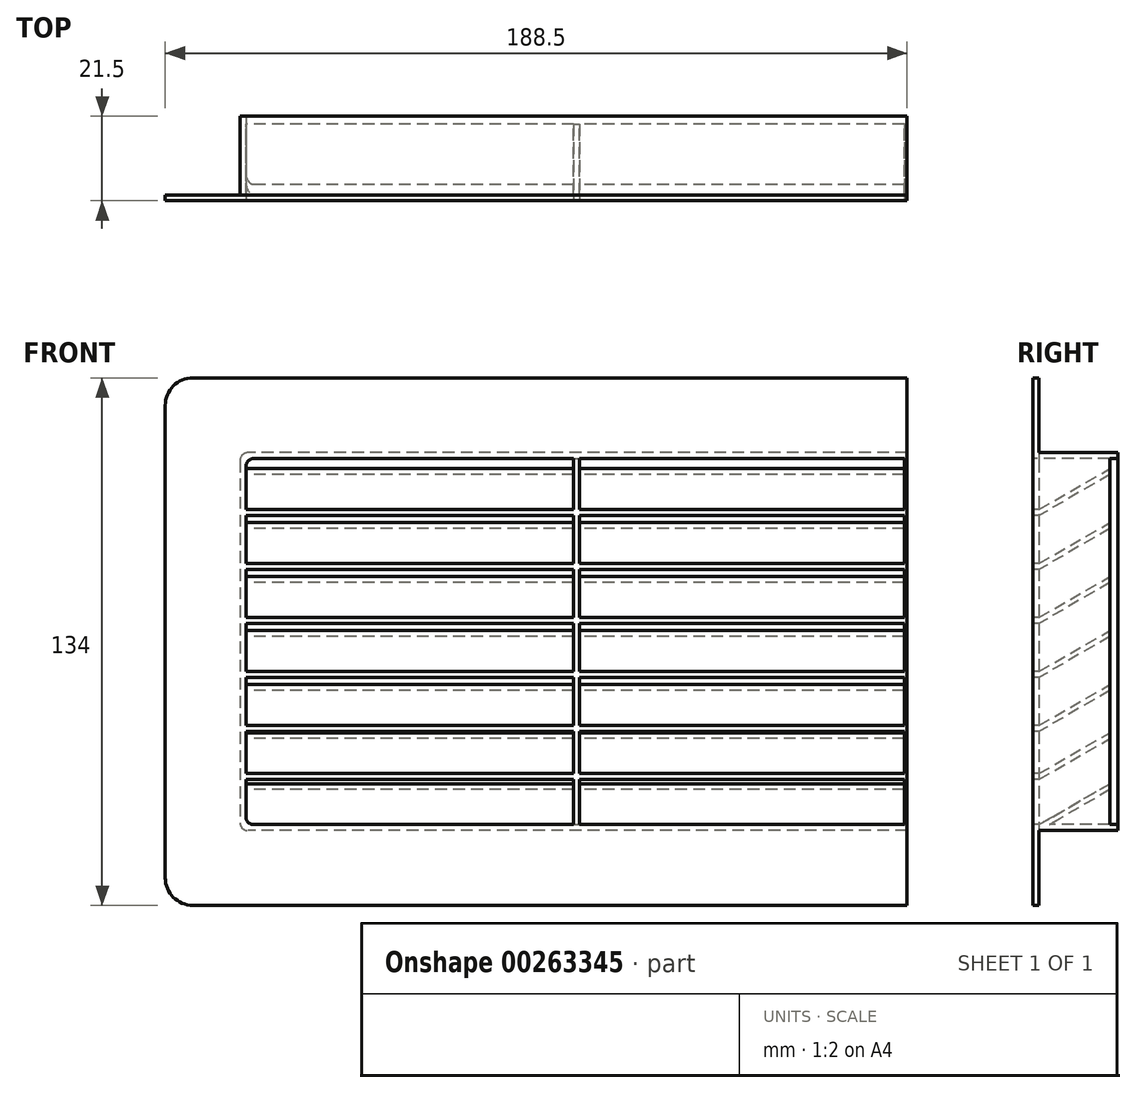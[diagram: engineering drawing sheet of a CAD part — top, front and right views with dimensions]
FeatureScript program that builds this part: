
annotation { "Feature Type Name" : "Feature", "Feature Type Description" : "" }
export const myFeature = defineFeature(function(context is Context, id is Id, definition is map)
    precondition{}
    {
        {
            var Q0;
            Q0=qCreatedBy(makeId("Front.planeOp"),FACE);
            var sketch = newSketch(context, id + "F0", { "sketchPlane" : qUnion([Q0])});
            skLineSegment(sketch, "E0.bottom", {"start": v(-180, 65) * mm, "end": v(180, 65) * mm});
            skLineSegment(sketch, "E0.top", {"start": v(-180, -65) * mm, "end": v(180, -65) * mm});
            skLineSegment(sketch, "E0.left", {"start": v(-185, 60) * mm, "end": v(-185, -60) * mm});
            skLineSegment(sketch, "E0.right", {"start": v(185, 60) * mm, "end": v(185, -60) * mm});
            skPoint(sketch, "E0.middle", {"position": v(0, 0) * mm});
            skPoint(sketch, "E1.visualSharp", {"position": v(-185, 65) * mm});
            skArc(sketch, "E1.filletArc", {"start": v(-180, 65) * mm, "mid": v(-183.54, 63.54) * mm, "end": v(-185, 60) * mm});
            skPoint(sketch, "E2.visualSharp", {"position": v(185, 65) * mm});
            skArc(sketch, "E2.filletArc", {"start": v(185, 60) * mm, "mid": v(183.54, 63.54) * mm, "end": v(180, 65) * mm});
            skPoint(sketch, "E3.visualSharp", {"position": v(185, -65) * mm});
            skArc(sketch, "E3.filletArc", {"start": v(180, -65) * mm, "mid": v(183.54, -63.54) * mm, "end": v(185, -60) * mm});
            skPoint(sketch, "E4.visualSharp", {"position": v(-185, -65) * mm});
            skArc(sketch, "E4.filletArc", {"start": v(-185, -60) * mm, "mid": v(-183.54, -63.54) * mm, "end": v(-180, -65) * mm});
            skSolve(sketch);
        }
        {
            var Q0;
            Q0=qSketchRegion(id+"F0",true);
            extrude(context, id + "F1", {"entities" : qUnion([Q0]), "depth" : 1.5 * mm});
        }
        {
            var Q0;
            Q0=makeQuery(id+"F1.opExtrude","CAP_FACE",FACE,{"disambiguationData":[OSD([sQuery(id+"F0.wireOp",EDGE,"E0.bottom"),sQuery(id+"F0.wireOp",EDGE,"E0.top"),sQuery(id+"F0.wireOp",EDGE,"E0.left"),sQuery(id+"F0.wireOp",EDGE,"E0.right")])],"isStart":false});
            var sketch = newSketch(context, id + "F2", { "sketchPlane" : qUnion([Q0])});
            skLineSegment(sketch, "E5.bottom", {"start": v(-166.5, 46.5) * mm, "end": v(-83.25, 46.5) * mm});
            skLineSegment(sketch, "E5.top", {"start": v(-166.5, -46.5) * mm, "end": v(-83.25, -46.5) * mm});
            skLineSegment(sketch, "E5.left", {"start": v(-166.5, 46.5) * mm, "end": v(-166.5, 33.54) * mm});
            skLineSegment(sketch, "E5.right", {"start": v(166.5, 46.5) * mm, "end": v(166.5, 33.54) * mm});
            skPoint(sketch, "E5.middle", {"position": v(0, 0) * mm});
            skLineSegment(sketch, "E6.0", {"start": v(-166.5, 32.04) * mm, "end": v(-83.25, 32.04) * mm});
            skLineSegment(sketch, "E7.0", {"start": v(-166.5, 18.32) * mm, "end": v(-83.25, 18.32) * mm});
            skLineSegment(sketch, "E8.0", {"start": v(-166.5, 4.6) * mm, "end": v(-83.25, 4.6) * mm});
            skLineSegment(sketch, "E9.0", {"start": v(-166.5, -9.1) * mm, "end": v(-83.25, -9.1) * mm});
            skLineSegment(sketch, "E10.0", {"start": v(-166.5, -22.82) * mm, "end": v(-83.25, -22.82) * mm});
            skLineSegment(sketch, "E11.0", {"start": v(-166.5, -33.54) * mm, "end": v(-83.25, -33.54) * mm});
            skLineSegment(sketch, "E12.0", {"start": v(-166.5, 33.54) * mm, "end": v(-83.25, 33.54) * mm});
            skLineSegment(sketch, "E13.0", {"start": v(-166.5, 19.82) * mm, "end": v(-83.25, 19.82) * mm});
            skLineSegment(sketch, "E14.0", {"start": v(-166.5, 6.1) * mm, "end": v(-83.25, 6.1) * mm});
            skLineSegment(sketch, "E15.0", {"start": v(-166.5, -7.6) * mm, "end": v(-83.25, -7.6) * mm});
            skLineSegment(sketch, "E16.0", {"start": v(-166.5, -21.32) * mm, "end": v(-83.25, -21.32) * mm});
            skLineSegment(sketch, "E17.0", {"start": v(-166.5, -35.04) * mm, "end": v(-83.25, -35.04) * mm});
            skLineSegment(sketch, "E18.0", {"start": v(-83.25, 46.5) * mm, "end": v(-83.25, 33.54) * mm});
            skLineSegment(sketch, "E19.0", {"start": v(-81.75, 46.5) * mm, "end": v(-81.75, 33.54) * mm});
            skLineSegment(sketch, "E20.0", {"start": v(0.75, 46.5) * mm, "end": v(0.75, 33.54) * mm});
            skLineSegment(sketch, "E21.0", {"start": v(2.25, 46.5) * mm, "end": v(2.25, 33.54) * mm});
            skLineSegment(sketch, "E22.0", {"start": v(84.75, 46.5) * mm, "end": v(84.75, 33.54) * mm});
            skLineSegment(sketch, "E23.0", {"start": v(86.25, 46.5) * mm, "end": v(86.25, 33.54) * mm});
            skLineSegment(sketch, "E24.trimOffspring", {"start": v(-81.75, 19.82) * mm, "end": v(0.75, 19.82) * mm});
            skLineSegment(sketch, "E25.trimOffspring", {"start": v(-81.75, 18.32) * mm, "end": v(0.75, 18.32) * mm});
            skLineSegment(sketch, "E26.trimOffspring", {"start": v(-81.75, 33.54) * mm, "end": v(0.75, 33.54) * mm});
            skLineSegment(sketch, "E27.trimOffspring", {"start": v(-81.75, 32.04) * mm, "end": v(0.75, 32.04) * mm});
            skLineSegment(sketch, "E28.trimOffspring", {"start": v(-83.25, 32.04) * mm, "end": v(-83.25, 19.82) * mm});
            skLineSegment(sketch, "E29.trimOffspring", {"start": v(-81.75, 32.04) * mm, "end": v(-81.75, 19.82) * mm});
            skLineSegment(sketch, "E30.trimOffspring", {"start": v(-166.5, 32.04) * mm, "end": v(-166.5, 19.82) * mm});
            skLineSegment(sketch, "E31.trimOffspring", {"start": v(-166.5, 18.32) * mm, "end": v(-166.5, 6.1) * mm});
            skLineSegment(sketch, "E32.trimOffspring", {"start": v(-81.75, 18.32) * mm, "end": v(-81.75, 6.1) * mm});
            skLineSegment(sketch, "E33.trimOffspring", {"start": v(-83.25, 18.32) * mm, "end": v(-83.25, 6.1) * mm});
            skLineSegment(sketch, "E34.trimOffspring", {"start": v(-83.25, 4.6) * mm, "end": v(-83.25, -7.6) * mm});
            skLineSegment(sketch, "E35.trimOffspring", {"start": v(-81.75, 4.6) * mm, "end": v(-81.75, -7.6) * mm});
            skLineSegment(sketch, "E36.trimOffspring", {"start": v(-81.75, 4.6) * mm, "end": v(0.75, 4.6) * mm});
            skLineSegment(sketch, "E37.trimOffspring", {"start": v(-81.75, 6.1) * mm, "end": v(0.75, 6.1) * mm});
            skLineSegment(sketch, "E38.trimOffspring", {"start": v(-166.5, 4.6) * mm, "end": v(-166.5, -7.6) * mm});
            skLineSegment(sketch, "E39.trimOffspring", {"start": v(-166.5, -9.1) * mm, "end": v(-166.5, -21.32) * mm});
            skLineSegment(sketch, "E40.trimOffspring", {"start": v(-83.25, -9.1) * mm, "end": v(-83.25, -21.32) * mm});
            skLineSegment(sketch, "E41.trimOffspring", {"start": v(-81.75, -9.1) * mm, "end": v(-81.75, -21.32) * mm});
            skLineSegment(sketch, "E42.trimOffspring", {"start": v(-81.75, -7.6) * mm, "end": v(0.75, -7.6) * mm});
            skLineSegment(sketch, "E43.trimOffspring", {"start": v(-81.75, -9.1) * mm, "end": v(0.75, -9.1) * mm});
            skLineSegment(sketch, "E44.trimOffspring", {"start": v(-166.5, -22.82) * mm, "end": v(-166.5, -33.54) * mm});
            skLineSegment(sketch, "E45.trimOffspring", {"start": v(-166.5, -35.04) * mm, "end": v(-166.5, -46.5) * mm});
            skLineSegment(sketch, "E46.trimOffspring", {"start": v(-83.25, -22.82) * mm, "end": v(-83.25, -33.54) * mm});
            skLineSegment(sketch, "E47.trimOffspring", {"start": v(-81.75, -22.82) * mm, "end": v(0.75, -22.82) * mm});
            skLineSegment(sketch, "E48.trimOffspring", {"start": v(-81.75, -21.32) * mm, "end": v(0.75, -21.32) * mm});
            skLineSegment(sketch, "E49.trimOffspring", {"start": v(-81.75, -22.82) * mm, "end": v(-81.75, -33.54) * mm});
            skLineSegment(sketch, "E50.trimOffspring", {"start": v(-83.25, -35.04) * mm, "end": v(-83.25, -46.5) * mm});
            skLineSegment(sketch, "E51.trimOffspring", {"start": v(-81.75, -35.04) * mm, "end": v(0.75, -35.04) * mm});
            skLineSegment(sketch, "E52.trimOffspring", {"start": v(-81.75, -33.54) * mm, "end": v(0.75, -33.54) * mm});
            skLineSegment(sketch, "E53.trimOffspring", {"start": v(-81.75, -35.04) * mm, "end": v(-81.75, -46.5) * mm});
            skLineSegment(sketch, "E54.trimOffspring", {"start": v(-81.75, -46.5) * mm, "end": v(0.75, -46.5) * mm});
            skLineSegment(sketch, "E55.trimOffspring", {"start": v(-81.75, 46.5) * mm, "end": v(0.75, 46.5) * mm});
            skLineSegment(sketch, "E56.trimOffspring", {"start": v(2.25, 46.5) * mm, "end": v(84.75, 46.5) * mm});
            skLineSegment(sketch, "E57.trimOffspring", {"start": v(2.25, 32.04) * mm, "end": v(84.75, 32.04) * mm});
            skLineSegment(sketch, "E58.trimOffspring", {"start": v(2.25, 33.54) * mm, "end": v(84.75, 33.54) * mm});
            skLineSegment(sketch, "E59.trimOffspring", {"start": v(2.25, 32.04) * mm, "end": v(2.25, 19.82) * mm});
            skLineSegment(sketch, "E60.trimOffspring", {"start": v(0.75, 32.04) * mm, "end": v(0.75, 19.82) * mm});
            skLineSegment(sketch, "E61.trimOffspring", {"start": v(2.25, 19.82) * mm, "end": v(84.75, 19.82) * mm});
            skLineSegment(sketch, "E62.trimOffspring", {"start": v(2.25, 18.32) * mm, "end": v(2.25, 6.1) * mm});
            skLineSegment(sketch, "E63.trimOffspring", {"start": v(2.25, 18.32) * mm, "end": v(84.75, 18.32) * mm});
            skLineSegment(sketch, "E64.trimOffspring", {"start": v(0.75, 18.32) * mm, "end": v(0.75, 6.1) * mm});
            skLineSegment(sketch, "E65.trimOffspring", {"start": v(2.25, 4.6) * mm, "end": v(2.25, -7.6) * mm});
            skLineSegment(sketch, "E66.trimOffspring", {"start": v(2.25, 6.1) * mm, "end": v(84.75, 6.1) * mm});
            skLineSegment(sketch, "E67.trimOffspring", {"start": v(0.75, 4.6) * mm, "end": v(0.75, -7.6) * mm});
            skLineSegment(sketch, "E68.trimOffspring", {"start": v(2.25, 4.6) * mm, "end": v(84.75, 4.6) * mm});
            skLineSegment(sketch, "E69.trimOffspring", {"start": v(2.25, -7.6) * mm, "end": v(84.75, -7.6) * mm});
            skLineSegment(sketch, "E70.trimOffspring", {"start": v(0.75, -9.1) * mm, "end": v(0.75, -21.32) * mm});
            skLineSegment(sketch, "E71.trimOffspring", {"start": v(2.25, -9.1) * mm, "end": v(2.25, -21.32) * mm});
            skLineSegment(sketch, "E72.trimOffspring", {"start": v(2.25, -9.1) * mm, "end": v(84.75, -9.1) * mm});
            skLineSegment(sketch, "E73.trimOffspring", {"start": v(2.25, -22.82) * mm, "end": v(2.25, -33.54) * mm});
            skLineSegment(sketch, "E74.trimOffspring", {"start": v(2.25, -21.32) * mm, "end": v(84.75, -21.32) * mm});
            skLineSegment(sketch, "E75.trimOffspring", {"start": v(0.75, -22.82) * mm, "end": v(0.75, -33.54) * mm});
            skLineSegment(sketch, "E76.trimOffspring", {"start": v(2.25, -22.82) * mm, "end": v(84.75, -22.82) * mm});
            skLineSegment(sketch, "E77.trimOffspring", {"start": v(2.25, -35.04) * mm, "end": v(84.75, -35.04) * mm});
            skLineSegment(sketch, "E78.trimOffspring", {"start": v(2.25, -35.04) * mm, "end": v(2.25, -46.5) * mm});
            skLineSegment(sketch, "E79.trimOffspring", {"start": v(2.25, -33.54) * mm, "end": v(84.75, -33.54) * mm});
            skLineSegment(sketch, "E80.trimOffspring", {"start": v(0.75, -35.04) * mm, "end": v(0.75, -46.5) * mm});
            skLineSegment(sketch, "E81.trimOffspring", {"start": v(2.25, -46.5) * mm, "end": v(84.75, -46.5) * mm});
            skLineSegment(sketch, "E82.trimOffspring", {"start": v(86.25, 46.5) * mm, "end": v(166.5, 46.5) * mm});
            skLineSegment(sketch, "E83.trimOffspring", {"start": v(86.25, 33.54) * mm, "end": v(166.5, 33.54) * mm});
            skLineSegment(sketch, "E84.trimOffspring", {"start": v(84.75, 32.04) * mm, "end": v(84.75, 19.82) * mm});
            skLineSegment(sketch, "E85.trimOffspring", {"start": v(86.25, 32.04) * mm, "end": v(86.25, 19.82) * mm});
            skLineSegment(sketch, "E86.trimOffspring", {"start": v(86.25, 32.04) * mm, "end": v(166.5, 32.04) * mm});
            skLineSegment(sketch, "E87.trimOffspring", {"start": v(84.75, 4.6) * mm, "end": v(84.75, -7.6) * mm});
            skLineSegment(sketch, "E88.trimOffspring", {"start": v(86.25, 4.6) * mm, "end": v(86.25, -7.6) * mm});
            skLineSegment(sketch, "E89.trimOffspring", {"start": v(86.25, 6.1) * mm, "end": v(166.5, 6.1) * mm});
            skLineSegment(sketch, "E90.trimOffspring", {"start": v(86.25, 4.6) * mm, "end": v(166.5, 4.6) * mm});
            skLineSegment(sketch, "E91.trimOffspring", {"start": v(86.25, 18.32) * mm, "end": v(166.5, 18.32) * mm});
            skLineSegment(sketch, "E92.trimOffspring", {"start": v(86.25, 18.32) * mm, "end": v(86.25, 6.1) * mm});
            skLineSegment(sketch, "E93.trimOffspring", {"start": v(84.75, 18.32) * mm, "end": v(84.75, 6.1) * mm});
            skLineSegment(sketch, "E94.trimOffspring", {"start": v(86.25, 19.82) * mm, "end": v(166.5, 19.82) * mm});
            skLineSegment(sketch, "E95.trimOffspring", {"start": v(86.25, -22.82) * mm, "end": v(166.5, -22.82) * mm});
            skLineSegment(sketch, "E96.trimOffspring", {"start": v(86.25, -22.82) * mm, "end": v(86.25, -33.54) * mm});
            skLineSegment(sketch, "E97.trimOffspring", {"start": v(84.75, -22.82) * mm, "end": v(84.75, -33.54) * mm});
            skLineSegment(sketch, "E98.trimOffspring", {"start": v(86.25, -9.1) * mm, "end": v(86.25, -21.32) * mm});
            skLineSegment(sketch, "E99.trimOffspring", {"start": v(84.75, -9.1) * mm, "end": v(84.75, -21.32) * mm});
            skLineSegment(sketch, "E100.trimOffspring", {"start": v(86.25, -7.6) * mm, "end": v(166.5, -7.6) * mm});
            skLineSegment(sketch, "E101.trimOffspring", {"start": v(86.25, -9.1) * mm, "end": v(166.5, -9.1) * mm});
            skLineSegment(sketch, "E102.trimOffspring", {"start": v(86.25, -21.32) * mm, "end": v(166.5, -21.32) * mm});
            skLineSegment(sketch, "E103.trimOffspring", {"start": v(86.25, -35.04) * mm, "end": v(86.25, -46.5) * mm});
            skLineSegment(sketch, "E104.trimOffspring", {"start": v(86.25, -35.04) * mm, "end": v(166.5, -35.04) * mm});
            skLineSegment(sketch, "E105.trimOffspring", {"start": v(86.25, -33.54) * mm, "end": v(166.5, -33.54) * mm});
            skLineSegment(sketch, "E106.trimOffspring", {"start": v(84.75, -35.04) * mm, "end": v(84.75, -46.5) * mm});
            skLineSegment(sketch, "E107.trimOffspring", {"start": v(86.25, -46.5) * mm, "end": v(166.5, -46.5) * mm});
            skLineSegment(sketch, "E108.trimOffspring", {"start": v(166.5, -35.04) * mm, "end": v(166.5, -46.5) * mm});
            skLineSegment(sketch, "E109.trimOffspring", {"start": v(166.5, -22.82) * mm, "end": v(166.5, -33.54) * mm});
            skLineSegment(sketch, "E110.trimOffspring", {"start": v(166.5, 32.04) * mm, "end": v(166.5, 19.82) * mm});
            skLineSegment(sketch, "E111.trimOffspring", {"start": v(166.5, 18.32) * mm, "end": v(166.5, 6.1) * mm});
            skLineSegment(sketch, "E112.trimOffspring", {"start": v(166.5, 4.6) * mm, "end": v(166.5, -7.6) * mm});
            skLineSegment(sketch, "E113.trimOffspring", {"start": v(166.5, -9.1) * mm, "end": v(166.5, -21.32) * mm});
            skSolve(sketch);
        }
        {
            var Q0;
            Q0=makeQuery(id+"F2.imprint","IMPRINT",FACE,{"disambiguationData":[TD([[makeQuery(id+"F2.imprint","IMPRINT",EDGE,{"derivedFrom":sQuery(id+"F2.wireOp",EDGE,"E5.bottom")}),-1.0]])]});
            var Q1;
            Q1=makeQuery(id+"F2.imprint","IMPRINT",FACE,{"disambiguationData":[TD([[makeQuery(id+"F2.imprint","IMPRINT",EDGE,{"derivedFrom":sQuery(id+"F2.wireOp",EDGE,"E19.0")}),1.0]])]});
            var Q2;
            Q2=makeQuery(id+"F2.imprint","IMPRINT",FACE,{"disambiguationData":[TD([[makeQuery(id+"F2.imprint","IMPRINT",EDGE,{"derivedFrom":sQuery(id+"F2.wireOp",EDGE,"E21.0")}),1.0]])]});
            var Q3;
            Q3=makeQuery(id+"F2.imprint","IMPRINT",FACE,{"disambiguationData":[TD([[makeQuery(id+"F2.imprint","IMPRINT",EDGE,{"derivedFrom":sQuery(id+"F2.wireOp",EDGE,"E5.right")}),-1.0]])]});
            var Q4;
            Q4=makeQuery(id+"F2.imprint","IMPRINT",FACE,{"disambiguationData":[TD([[makeQuery(id+"F2.imprint","IMPRINT",EDGE,{"derivedFrom":sQuery(id+"F2.wireOp",EDGE,"E6.0")}),-1.0]])]});
            var Q5;
            Q5=makeQuery(id+"F2.imprint","IMPRINT",FACE,{"disambiguationData":[TD([[makeQuery(id+"F2.imprint","IMPRINT",EDGE,{"derivedFrom":sQuery(id+"F2.wireOp",EDGE,"E24.trimOffspring")}),1.0]])]});
            var Q6;
            Q6=makeQuery(id+"F2.imprint","IMPRINT",FACE,{"disambiguationData":[TD([[makeQuery(id+"F2.imprint","IMPRINT",EDGE,{"derivedFrom":sQuery(id+"F2.wireOp",EDGE,"E57.trimOffspring")}),-1.0]])]});
            var Q7;
            Q7=makeQuery(id+"F2.imprint","IMPRINT",FACE,{"disambiguationData":[TD([[makeQuery(id+"F2.imprint","IMPRINT",EDGE,{"derivedFrom":sQuery(id+"F2.wireOp",EDGE,"E85.trimOffspring")}),1.0]])]});
            var Q8;
            Q8=makeQuery(id+"F2.imprint","IMPRINT",FACE,{"disambiguationData":[TD([[makeQuery(id+"F2.imprint","IMPRINT",EDGE,{"derivedFrom":sQuery(id+"F2.wireOp",EDGE,"E7.0")}),-1.0]])]});
            var Q9;
            Q9=makeQuery(id+"F2.imprint","IMPRINT",FACE,{"disambiguationData":[TD([[makeQuery(id+"F2.imprint","IMPRINT",EDGE,{"derivedFrom":sQuery(id+"F2.wireOp",EDGE,"E25.trimOffspring")}),-1.0]])]});
            var Q10;
            Q10=makeQuery(id+"F2.imprint","IMPRINT",FACE,{"disambiguationData":[TD([[makeQuery(id+"F2.imprint","IMPRINT",EDGE,{"derivedFrom":sQuery(id+"F2.wireOp",EDGE,"E62.trimOffspring")}),1.0]])]});
            var Q11;
            Q11=makeQuery(id+"F2.imprint","IMPRINT",FACE,{"disambiguationData":[TD([[makeQuery(id+"F2.imprint","IMPRINT",EDGE,{"derivedFrom":sQuery(id+"F2.wireOp",EDGE,"E89.trimOffspring")}),1.0]])]});
            var Q12;
            Q12=makeQuery(id+"F2.imprint","IMPRINT",FACE,{"disambiguationData":[TD([[makeQuery(id+"F2.imprint","IMPRINT",EDGE,{"derivedFrom":sQuery(id+"F2.wireOp",EDGE,"E8.0")}),-1.0]])]});
            var Q13;
            Q13=makeQuery(id+"F2.imprint","IMPRINT",FACE,{"disambiguationData":[TD([[makeQuery(id+"F2.imprint","IMPRINT",EDGE,{"derivedFrom":sQuery(id+"F2.wireOp",EDGE,"E35.trimOffspring")}),1.0]])]});
            var Q14;
            Q14=makeQuery(id+"F2.imprint","IMPRINT",FACE,{"disambiguationData":[TD([[makeQuery(id+"F2.imprint","IMPRINT",EDGE,{"derivedFrom":sQuery(id+"F2.wireOp",EDGE,"E65.trimOffspring")}),1.0]])]});
            var Q15;
            Q15=makeQuery(id+"F2.imprint","IMPRINT",FACE,{"disambiguationData":[TD([[makeQuery(id+"F2.imprint","IMPRINT",EDGE,{"derivedFrom":sQuery(id+"F2.wireOp",EDGE,"E88.trimOffspring")}),1.0]])]});
            var Q16;
            Q16=makeQuery(id+"F2.imprint","IMPRINT",FACE,{"disambiguationData":[TD([[makeQuery(id+"F2.imprint","IMPRINT",EDGE,{"derivedFrom":sQuery(id+"F2.wireOp",EDGE,"E9.0")}),-1.0]])]});
            var Q17;
            Q17=makeQuery(id+"F2.imprint","IMPRINT",FACE,{"disambiguationData":[TD([[makeQuery(id+"F2.imprint","IMPRINT",EDGE,{"derivedFrom":sQuery(id+"F2.wireOp",EDGE,"E41.trimOffspring")}),1.0]])]});
            var Q18;
            Q18=makeQuery(id+"F2.imprint","IMPRINT",FACE,{"disambiguationData":[TD([[makeQuery(id+"F2.imprint","IMPRINT",EDGE,{"derivedFrom":sQuery(id+"F2.wireOp",EDGE,"E71.trimOffspring")}),1.0]])]});
            var Q19;
            Q19=makeQuery(id+"F2.imprint","IMPRINT",FACE,{"disambiguationData":[TD([[makeQuery(id+"F2.imprint","IMPRINT",EDGE,{"derivedFrom":sQuery(id+"F2.wireOp",EDGE,"E98.trimOffspring")}),1.0]])]});
            var Q20;
            Q20=makeQuery(id+"F2.imprint","IMPRINT",FACE,{"disambiguationData":[TD([[makeQuery(id+"F2.imprint","IMPRINT",EDGE,{"derivedFrom":sQuery(id+"F2.wireOp",EDGE,"E10.0")}),-1.0]])]});
            var Q21;
            Q21=makeQuery(id+"F2.imprint","IMPRINT",FACE,{"disambiguationData":[TD([[makeQuery(id+"F2.imprint","IMPRINT",EDGE,{"derivedFrom":sQuery(id+"F2.wireOp",EDGE,"E47.trimOffspring")}),-1.0]])]});
            var Q22;
            Q22=makeQuery(id+"F2.imprint","IMPRINT",FACE,{"disambiguationData":[TD([[makeQuery(id+"F2.imprint","IMPRINT",EDGE,{"derivedFrom":sQuery(id+"F2.wireOp",EDGE,"E73.trimOffspring")}),1.0]])]});
            var Q23;
            Q23=makeQuery(id+"F2.imprint","IMPRINT",FACE,{"disambiguationData":[TD([[makeQuery(id+"F2.imprint","IMPRINT",EDGE,{"derivedFrom":sQuery(id+"F2.wireOp",EDGE,"E95.trimOffspring")}),-1.0]])]});
            var Q24;
            Q24=makeQuery(id+"F2.imprint","IMPRINT",FACE,{"disambiguationData":[TD([[makeQuery(id+"F2.imprint","IMPRINT",EDGE,{"derivedFrom":sQuery(id+"F2.wireOp",EDGE,"E5.top")}),1.0]])]});
            var Q25;
            Q25=makeQuery(id+"F2.imprint","IMPRINT",FACE,{"disambiguationData":[TD([[makeQuery(id+"F2.imprint","IMPRINT",EDGE,{"derivedFrom":sQuery(id+"F2.wireOp",EDGE,"E51.trimOffspring")}),-1.0]])]});
            var Q26;
            Q26=makeQuery(id+"F2.imprint","IMPRINT",FACE,{"disambiguationData":[TD([[makeQuery(id+"F2.imprint","IMPRINT",EDGE,{"derivedFrom":sQuery(id+"F2.wireOp",EDGE,"E77.trimOffspring")}),-1.0]])]});
            var Q27;
            Q27=makeQuery(id+"F2.imprint","IMPRINT",FACE,{"disambiguationData":[TD([[makeQuery(id+"F2.imprint","IMPRINT",EDGE,{"derivedFrom":sQuery(id+"F2.wireOp",EDGE,"E103.trimOffspring")}),1.0]])]});
            extrude(context, id + "F3", {"entities" : qUnion([Q0, Q1, Q2, Q3, Q4, Q5, Q6, Q7, Q8, Q9, Q10, Q11, Q12, Q13, Q14, Q15, Q16, Q17, Q18, Q19, Q20, Q21, Q22, Q23, Q24, Q25, Q26, Q27]), "operationType" : NewBodyOperationType.REMOVE, "endBound" : BoundingType.THROUGH_ALL, "oppositeDirection" : true, "depth" : 25 * mm});
        }
        {
            var Q0;
            Q0=makeQuery(id+"F1.opExtrude","CAP_FACE",FACE,{"disambiguationData":[OSD([sQuery(id+"F0.wireOp",EDGE,"E0.bottom"),sQuery(id+"F0.wireOp",EDGE,"E0.top"),sQuery(id+"F0.wireOp",EDGE,"E0.left"),sQuery(id+"F0.wireOp",EDGE,"E0.right")])],"isStart":true});
            var sketch = newSketch(context, id + "F4", { "sketchPlane" : qUnion([Q0])});
            skLineSegment(sketch, "E114.bottom", {"start": v(-166.5, 46.5) * mm, "end": v(166.5, 46.5) * mm});
            skLineSegment(sketch, "E114.top", {"start": v(-166.5, -46.5) * mm, "end": v(166.5, -46.5) * mm});
            skLineSegment(sketch, "E114.left", {"start": v(-166.5, 46.5) * mm, "end": v(-166.5, -46.5) * mm});
            skLineSegment(sketch, "E114.right", {"start": v(166.5, 46.5) * mm, "end": v(166.5, -46.5) * mm});
            skPoint(sketch, "E114.middle", {"position": v(0, 0) * mm});
            skLineSegment(sketch, "E115.0", {"start": v(-168, 48) * mm, "end": v(168, 48) * mm});
            skLineSegment(sketch, "E115.1", {"start": v(-168, 48) * mm, "end": v(-168, -48) * mm});
            skLineSegment(sketch, "E115.2", {"start": v(-168, -48) * mm, "end": v(168, -48) * mm});
            skLineSegment(sketch, "E115.3", {"start": v(168, 48) * mm, "end": v(168, -48) * mm});
            skSolve(sketch);
        }
        {
            var Q0;
            Q0=qSketchRegion(id+"F4",true);
            extrude(context, id + "F5", {"entities" : qUnion([Q0]), "operationType" : NewBodyOperationType.ADD, "depth" : 20 * mm});
        }
        {
            var Q0;
            Q0=makeQuery(id+"F5.boolean.opBoolean","MERGE",FACE,{"derivedFrom":[makeQuery(id+"F3.boolean.opBoolean","COPY",FACE,{"derivedFrom":makeQuery(id+"F3.opExtrude","SWEPT_FACE",FACE,{"disambiguationData":[OSD([sQuery(id+"F2.wireOp",EDGE,"E5.left")])]})}),makeQuery(id+"F3.boolean.opBoolean","COPY",FACE,{"derivedFrom":makeQuery(id+"F3.opExtrude","SWEPT_FACE",FACE,{"disambiguationData":[OSD([sQuery(id+"F2.wireOp",EDGE,"E30.trimOffspring")])]})}),makeQuery(id+"F3.boolean.opBoolean","COPY",FACE,{"derivedFrom":makeQuery(id+"F3.opExtrude","SWEPT_FACE",FACE,{"disambiguationData":[OSD([sQuery(id+"F2.wireOp",EDGE,"E31.trimOffspring")])]})}),makeQuery(id+"F3.boolean.opBoolean","COPY",FACE,{"derivedFrom":makeQuery(id+"F3.opExtrude","SWEPT_FACE",FACE,{"disambiguationData":[OSD([sQuery(id+"F2.wireOp",EDGE,"E38.trimOffspring")])]})}),makeQuery(id+"F3.boolean.opBoolean","COPY",FACE,{"derivedFrom":makeQuery(id+"F3.opExtrude","SWEPT_FACE",FACE,{"disambiguationData":[OSD([sQuery(id+"F2.wireOp",EDGE,"E39.trimOffspring")])]})}),makeQuery(id+"F3.boolean.opBoolean","COPY",FACE,{"derivedFrom":makeQuery(id+"F3.opExtrude","SWEPT_FACE",FACE,{"disambiguationData":[OSD([sQuery(id+"F2.wireOp",EDGE,"E44.trimOffspring")])]})}),makeQuery(id+"F3.boolean.opBoolean","COPY",FACE,{"derivedFrom":makeQuery(id+"F3.opExtrude","SWEPT_FACE",FACE,{"disambiguationData":[OSD([sQuery(id+"F2.wireOp",EDGE,"E45.trimOffspring")])]})}),makeQuery(id+"F5.opExtrude","SWEPT_FACE",FACE,{"disambiguationData":[OSD([sQuery(id+"F4.wireOp",EDGE,"E114.right")])]})]});
            var sketch = newSketch(context, id + "F6", { "sketchPlane" : qUnion([Q0])});
            skLineSegment(sketch, "E116", {"start": v(0, 46.5) * mm, "end": v(0, -35.04) * mm, "construction": true});
            skPoint(sketch, "E116.endSnap0", {"position": v(0, 19.07) * mm});
            skLineSegment(sketch, "E117", {"start": v(0, 33.54) * mm, "end": v(18, 43.93) * mm});
            skLineSegment(sketch, "E118", {"start": v(18, 43.93) * mm, "end": v(18, 42.43) * mm});
            skLineSegment(sketch, "E119", {"start": v(18, 42.43) * mm, "end": v(0, 32.04) * mm});
            skLineSegment(sketch, "E120", {"start": v(0, 32.04) * mm, "end": v(0, 33.54) * mm});
            skLineSegment(sketch, "E121", {"start": v(0, 33.54) * mm, "end": v(0, 32.04) * mm});
            skLineSegment(sketch, "E122.0.1.0", {"start": v(0, 19.82) * mm, "end": v(18, 30.21) * mm});
            skLineSegment(sketch, "E122.0.1.1", {"start": v(18, 28.71) * mm, "end": v(0, 18.32) * mm});
            skLineSegment(sketch, "E122.0.1.2", {"start": v(18, 30.21) * mm, "end": v(18, 28.71) * mm});
            skLineSegment(sketch, "E122.0.2.0", {"start": v(0, 6.1) * mm, "end": v(18, 16.5) * mm});
            skLineSegment(sketch, "E122.0.2.1", {"start": v(18, 15) * mm, "end": v(0, 4.6) * mm});
            skLineSegment(sketch, "E122.0.2.2", {"start": v(18, 16.5) * mm, "end": v(18, 15) * mm});
            skLineSegment(sketch, "E122.0.3.0", {"start": v(0, -7.6) * mm, "end": v(18, 2.79) * mm});
            skLineSegment(sketch, "E122.0.3.1", {"start": v(18, 1.29) * mm, "end": v(0, -9.1) * mm});
            skLineSegment(sketch, "E122.0.3.2", {"start": v(18, 2.79) * mm, "end": v(18, 1.29) * mm});
            skLineSegment(sketch, "E122.0.4.0", {"start": v(0, -21.32) * mm, "end": v(18, -10.93) * mm});
            skLineSegment(sketch, "E122.0.4.1", {"start": v(18, -12.43) * mm, "end": v(0, -22.82) * mm});
            skLineSegment(sketch, "E122.0.4.2", {"start": v(18, -10.93) * mm, "end": v(18, -12.43) * mm});
            skLineSegment(sketch, "E122.0.5.0", {"start": v(0, -35.04) * mm, "end": v(18, -24.64) * mm});
            skLineSegment(sketch, "E122.direction1", {"start": v(0, 33.54) * mm, "end": v(0, 33.54) * mm});
            skLineSegment(sketch, "E122.direction2", {"start": v(0, 33.54) * mm, "end": v(0, 19.82) * mm, "construction": true});
            skLineSegment(sketch, "E123", {"start": v(0, 19.82) * mm, "end": v(0, 18.32) * mm});
            skLineSegment(sketch, "E124", {"start": v(0, 6.1) * mm, "end": v(0, 4.6) * mm});
            skLineSegment(sketch, "E125", {"start": v(0, -33.54) * mm, "end": v(18, -23.14) * mm});
            skLineSegment(sketch, "E126", {"start": v(18, -23.14) * mm, "end": v(18, -24.64) * mm});
            skLineSegment(sketch, "E127.trimOffspring", {"start": v(0, -35.04) * mm, "end": v(0, -46.5) * mm, "construction": true});
            skLineSegment(sketch, "E128", {"start": v(0, -35.04) * mm, "end": v(0, -33.54) * mm});
            skLineSegment(sketch, "E129", {"start": v(0, -21.32) * mm, "end": v(0, -22.82) * mm});
            skLineSegment(sketch, "E130", {"start": v(0, -46.5) * mm, "end": v(18, -36.1) * mm});
            skLineSegment(sketch, "E131", {"start": v(18, -36.1) * mm, "end": v(18, -37.6) * mm});
            skLineSegment(sketch, "E132", {"start": v(18, -37.6) * mm, "end": v(2.6, -46.5) * mm});
            skLineSegment(sketch, "E133", {"start": v(2.6, -46.5) * mm, "end": v(0, -46.5) * mm});
            skLineSegment(sketch, "E134", {"start": v(0, -7.6) * mm, "end": v(0, -9.1) * mm});
            skSolve(sketch);
        }
        {
            var Q0;
            Q0=makeQuery(id+"F5.boolean.opBoolean","SPLIT",FACE,{"disambiguationData":[TD([makeQuery(id+"F3.boolean.opBoolean","COPY",FACE,{"derivedFrom":makeQuery(id+"F3.opExtrude","SWEPT_FACE",FACE,{"disambiguationData":[OSD([sQuery(id+"F2.wireOp",EDGE,"E5.bottom")])]})})])],"derivedFrom":makeQuery(id+"F1.opExtrude","CAP_FACE",FACE,{"disambiguationData":[OSD([sQuery(id+"F0.wireOp",EDGE,"E0.bottom"),sQuery(id+"F0.wireOp",EDGE,"E0.top"),sQuery(id+"F0.wireOp",EDGE,"E0.left"),sQuery(id+"F0.wireOp",EDGE,"E0.right")])],"isStart":true})});
            var sketch = newSketch(context, id + "F7", { "sketchPlane" : qUnion([Q0])});
            skLineSegment(sketch, "E135.bottom", {"start": v(-86.25, 46.5) * mm, "end": v(-84.75, 46.5) * mm});
            skLineSegment(sketch, "E135.top", {"start": v(-86.25, -46.5) * mm, "end": v(-84.75, -46.5) * mm});
            skLineSegment(sketch, "E135.left", {"start": v(-86.25, 46.5) * mm, "end": v(-86.25, -46.5) * mm});
            skLineSegment(sketch, "E135.right", {"start": v(-84.75, 46.5) * mm, "end": v(-84.75, -46.5) * mm});
            skLineSegment(sketch, "E136.bottom", {"start": v(-2.25, 46.5) * mm, "end": v(-0.75, 46.5) * mm});
            skLineSegment(sketch, "E136.top", {"start": v(-2.25, -46.5) * mm, "end": v(-0.75, -46.5) * mm});
            skLineSegment(sketch, "E136.left", {"start": v(-2.25, 46.5) * mm, "end": v(-2.25, -46.5) * mm});
            skLineSegment(sketch, "E136.right", {"start": v(-0.75, 46.5) * mm, "end": v(-0.75, -46.5) * mm});
            skLineSegment(sketch, "E137.bottom", {"start": v(81.75, 46.5) * mm, "end": v(83.25, 46.5) * mm});
            skLineSegment(sketch, "E137.top", {"start": v(81.75, -46.5) * mm, "end": v(83.25, -46.5) * mm});
            skLineSegment(sketch, "E137.left", {"start": v(81.75, 46.5) * mm, "end": v(81.75, -46.5) * mm});
            skLineSegment(sketch, "E137.right", {"start": v(83.25, 46.5) * mm, "end": v(83.25, -46.5) * mm});
            skSolve(sketch);
        }
        {
            var Q0;
            Q0=qSketchRegion(id+"F7",true);
            extrude(context, id + "F8", {"entities" : qUnion([Q0]), "operationType" : NewBodyOperationType.ADD, "depth" : 18 * mm});
        }
        {
            var Q0;
            Q0=qSketchRegion(id+"F6",true);
            var Q1;
            Q1=makeQuery(id+"F5.boolean.opBoolean","MERGE",FACE,{"derivedFrom":[makeQuery(id+"F3.boolean.opBoolean","COPY",FACE,{"derivedFrom":makeQuery(id+"F3.opExtrude","SWEPT_FACE",FACE,{"disambiguationData":[OSD([sQuery(id+"F2.wireOp",EDGE,"E5.right")])]})}),makeQuery(id+"F3.boolean.opBoolean","COPY",FACE,{"derivedFrom":makeQuery(id+"F3.opExtrude","SWEPT_FACE",FACE,{"disambiguationData":[OSD([sQuery(id+"F2.wireOp",EDGE,"E108.trimOffspring")])]})}),makeQuery(id+"F3.boolean.opBoolean","COPY",FACE,{"derivedFrom":makeQuery(id+"F3.opExtrude","SWEPT_FACE",FACE,{"disambiguationData":[OSD([sQuery(id+"F2.wireOp",EDGE,"E109.trimOffspring")])]})}),makeQuery(id+"F3.boolean.opBoolean","COPY",FACE,{"derivedFrom":makeQuery(id+"F3.opExtrude","SWEPT_FACE",FACE,{"disambiguationData":[OSD([sQuery(id+"F2.wireOp",EDGE,"E110.trimOffspring")])]})}),makeQuery(id+"F3.boolean.opBoolean","COPY",FACE,{"derivedFrom":makeQuery(id+"F3.opExtrude","SWEPT_FACE",FACE,{"disambiguationData":[OSD([sQuery(id+"F2.wireOp",EDGE,"E111.trimOffspring")])]})}),makeQuery(id+"F3.boolean.opBoolean","COPY",FACE,{"derivedFrom":makeQuery(id+"F3.opExtrude","SWEPT_FACE",FACE,{"disambiguationData":[OSD([sQuery(id+"F2.wireOp",EDGE,"E112.trimOffspring")])]})}),makeQuery(id+"F3.boolean.opBoolean","COPY",FACE,{"derivedFrom":makeQuery(id+"F3.opExtrude","SWEPT_FACE",FACE,{"disambiguationData":[OSD([sQuery(id+"F2.wireOp",EDGE,"E113.trimOffspring")])]})}),makeQuery(id+"F5.opExtrude","SWEPT_FACE",FACE,{"disambiguationData":[OSD([sQuery(id+"F4.wireOp",EDGE,"E114.left")])]})]});
            extrude(context, id + "F9", {"entities" : qUnion([Q0]), "operationType" : NewBodyOperationType.ADD, "endBound" : BoundingType.UP_TO_SURFACE, "endBoundEntityFace" : qUnion([Q1]), "depth" : 25 * mm});
        }
        {
            var Q0;
            Q0=makeQuery(id+"F5.opExtrude","SWEPT_EDGE",EDGE,{"disambiguationData":[OSD([sQuery(id+"F4.wireOp",EDGE,"E115.1"),sQuery(id+"F4.wireOp",EDGE,"E115.2")])]});
            var Q1;
            Q1=makeQuery(id+"F5.opExtrude","SWEPT_EDGE",EDGE,{"disambiguationData":[OSD([sQuery(id+"F4.wireOp",EDGE,"E115.0"),sQuery(id+"F4.wireOp",EDGE,"E115.1")])]});
            var Q2;
            Q2=makeQuery(id+"F5.opExtrude","SWEPT_EDGE",EDGE,{"disambiguationData":[OSD([sQuery(id+"F4.wireOp",EDGE,"E115.2"),sQuery(id+"F4.wireOp",EDGE,"E115.3")])]});
            var Q3;
            Q3=makeQuery(id+"F5.opExtrude","SWEPT_EDGE",EDGE,{"disambiguationData":[OSD([sQuery(id+"F4.wireOp",EDGE,"E115.0"),sQuery(id+"F4.wireOp",EDGE,"E115.3")])]});
            fillet(context, id + "F10", {"entities" : qUnion([Q0, Q1, Q2, Q3]), "radius" : 2 * mm, "tangentPropagation" : true, "allowEdgeOverflow" : false});
        }
        {
            var Q0;
            Q0=makeQuery(id+"F5.boolean.opBoolean","MERGE",EDGE,{"derivedFrom":[makeQuery(id+"F3.boolean.opBoolean","COPY",EDGE,{"derivedFrom":makeQuery(id+"F3.opExtrude","SWEPT_EDGE",EDGE,{"disambiguationData":[OSD([sQuery(id+"F2.wireOp",EDGE,"E5.bottom"),sQuery(id+"F2.wireOp",EDGE,"E5.left")])]})}),makeQuery(id+"F5.opExtrude","SWEPT_EDGE",EDGE,{"disambiguationData":[OSD([sQuery(id+"F4.wireOp",EDGE,"E114.bottom"),sQuery(id+"F4.wireOp",EDGE,"E114.right")])]})]});
            fillet(context, id + "F11", {"entities" : qUnion([Q0]), "radius" : 2 * mm, "tangentPropagation" : true, "allowEdgeOverflow" : false});
        }
        {
            var Q0;
            {var subQ0=sQuery(id+"F2.wireOp",EDGE,"E45.trimOffspring");var subQ1=sQuery(id+"F2.wireOp",EDGE,"E5.top");var subQ2=sQuery(id+"F4.wireOp",EDGE,"E114.right");var subQ3=sQuery(id+"F4.wireOp",EDGE,"E114.top");Q0=makeQuery(id+"F9.boolean.opBoolean","SPLIT",EDGE,{"disambiguationData":[TD([makeQuery(id+"F9.opExtrude","SWEPT_FACE",FACE,{"disambiguationData":[OSD([sQuery(id+"F6.wireOp",EDGE,"E132")])]})])],"derivedFrom":makeQuery(id+"F5.boolean.opBoolean","MERGE",EDGE,{"derivedFrom":[makeQuery(id+"F3.boolean.opBoolean","COPY",EDGE,{"derivedFrom":makeQuery(id+"F3.opExtrude","SWEPT_EDGE",EDGE,{"disambiguationData":[OSD([subQ1,subQ0])]})}),makeQuery(id+"F5.opExtrude","SWEPT_EDGE",EDGE,{"disambiguationData":[OSD([subQ3,subQ2])]})]})});}
            var Q1;
            {var subQ0=sQuery(id+"F2.wireOp",EDGE,"E108.trimOffspring");var subQ1=sQuery(id+"F2.wireOp",EDGE,"E107.trimOffspring");var subQ2=sQuery(id+"F4.wireOp",EDGE,"E114.left");var subQ3=sQuery(id+"F4.wireOp",EDGE,"E114.top");Q1=makeQuery(id+"F9.boolean.opBoolean","SPLIT",EDGE,{"disambiguationData":[TD([makeQuery(id+"F9.opExtrude","SWEPT_FACE",FACE,{"disambiguationData":[OSD([sQuery(id+"F6.wireOp",EDGE,"E132")])]})])],"derivedFrom":makeQuery(id+"F5.boolean.opBoolean","MERGE",EDGE,{"derivedFrom":[makeQuery(id+"F3.boolean.opBoolean","COPY",EDGE,{"derivedFrom":makeQuery(id+"F3.opExtrude","SWEPT_EDGE",EDGE,{"disambiguationData":[OSD([subQ1,subQ0])]})}),makeQuery(id+"F5.opExtrude","SWEPT_EDGE",EDGE,{"disambiguationData":[OSD([subQ3,subQ2])]})]})});}
            var Q2;
            Q2=makeQuery(id+"F5.boolean.opBoolean","MERGE",EDGE,{"derivedFrom":[makeQuery(id+"F3.boolean.opBoolean","COPY",EDGE,{"derivedFrom":makeQuery(id+"F3.opExtrude","SWEPT_EDGE",EDGE,{"disambiguationData":[OSD([sQuery(id+"F2.wireOp",EDGE,"E5.right"),sQuery(id+"F2.wireOp",EDGE,"E82.trimOffspring")])]})}),makeQuery(id+"F5.opExtrude","SWEPT_EDGE",EDGE,{"disambiguationData":[OSD([sQuery(id+"F4.wireOp",EDGE,"E114.bottom"),sQuery(id+"F4.wireOp",EDGE,"E114.left")])]})]});
            fillet(context, id + "F12", {"entities" : qUnion([Q0, Q1, Q2]), "radius" : 2 * mm, "tangentPropagation" : true, "allowEdgeOverflow" : false});
        }
        {
            var Q0;
            {var subQ0=sQuery(id+"F2.wireOp",EDGE,"E45.trimOffspring");var subQ1=sQuery(id+"F4.wireOp",EDGE,"E114.right");var subQ2=sQuery(id+"F2.wireOp",EDGE,"E5.top");var subQ3=sQuery(id+"F4.wireOp",EDGE,"E114.top");Q0=makeQuery(id+"F9.boolean.opBoolean","SPLIT",EDGE,{"disambiguationData":[TD([makeQuery(id+"F9.opExtrude","SWEPT_FACE",FACE,{"disambiguationData":[OSD([sQuery(id+"F6.wireOp",EDGE,"E130")])]})])],"derivedFrom":makeQuery(id+"F5.boolean.opBoolean","MERGE",EDGE,{"derivedFrom":[makeQuery(id+"F3.boolean.opBoolean","COPY",EDGE,{"derivedFrom":makeQuery(id+"F3.opExtrude","SWEPT_EDGE",EDGE,{"disambiguationData":[OSD([subQ2,subQ0])]})}),makeQuery(id+"F5.opExtrude","SWEPT_EDGE",EDGE,{"disambiguationData":[OSD([subQ3,subQ1])]})]})});}
            var Q1;
            {var subQ0=sQuery(id+"F2.wireOp",EDGE,"E108.trimOffspring");var subQ1=sQuery(id+"F2.wireOp",EDGE,"E107.trimOffspring");var subQ2=sQuery(id+"F4.wireOp",EDGE,"E114.top");var subQ3=sQuery(id+"F4.wireOp",EDGE,"E114.left");Q1=makeQuery(id+"F9.boolean.opBoolean","SPLIT",EDGE,{"disambiguationData":[TD([makeQuery(id+"F9.opExtrude","SWEPT_FACE",FACE,{"disambiguationData":[OSD([sQuery(id+"F6.wireOp",EDGE,"E130")])]})])],"derivedFrom":makeQuery(id+"F5.boolean.opBoolean","MERGE",EDGE,{"derivedFrom":[makeQuery(id+"F3.boolean.opBoolean","COPY",EDGE,{"derivedFrom":makeQuery(id+"F3.opExtrude","SWEPT_EDGE",EDGE,{"disambiguationData":[OSD([subQ1,subQ0])]})}),makeQuery(id+"F5.opExtrude","SWEPT_EDGE",EDGE,{"disambiguationData":[OSD([subQ2,subQ3])]})]})});}
            fillet(context, id + "F13", {"entities" : qUnion([Q0, Q1]), "radius" : 2 * mm, "tangentPropagation" : true, "allowEdgeOverflow" : false});
        }
        {
            var Q0;
            Q0=makeQuery(id+"F3.boolean.opBoolean","COPY",EDGE,{"derivedFrom":makeQuery(id+"F3.opExtrude","CAP_EDGE",EDGE,{"disambiguationData":[OSD([sQuery(id+"F2.wireOp",EDGE,"E55.trimOffspring")])],"isStart":true})});
            var Q1;
            Q1=makeQuery(id+"F3.boolean.opBoolean","COPY",EDGE,{"derivedFrom":makeQuery(id+"F3.opExtrude","CAP_EDGE",EDGE,{"disambiguationData":[OSD([sQuery(id+"F2.wireOp",EDGE,"E56.trimOffspring")])],"isStart":true})});
            var Q2;
            Q2=makeQuery(id+"F3.boolean.opBoolean","COPY",EDGE,{"derivedFrom":makeQuery(id+"F3.opExtrude","CAP_EDGE",EDGE,{"disambiguationData":[OSD([sQuery(id+"F2.wireOp",EDGE,"E82.trimOffspring")])],"isStart":true})});
            var Q3;
            Q3=makeQuery(id+"F3.boolean.opBoolean","COPY",EDGE,{"derivedFrom":makeQuery(id+"F3.opExtrude","CAP_EDGE",EDGE,{"disambiguationData":[OSD([sQuery(id+"F2.wireOp",EDGE,"E110.trimOffspring")])],"isStart":true})});
            var Q4;
            Q4=makeQuery(id+"F3.boolean.opBoolean","COPY",EDGE,{"derivedFrom":makeQuery(id+"F3.opExtrude","CAP_EDGE",EDGE,{"disambiguationData":[OSD([sQuery(id+"F2.wireOp",EDGE,"E111.trimOffspring")])],"isStart":true})});
            var Q5;
            Q5=makeQuery(id+"F3.boolean.opBoolean","COPY",EDGE,{"derivedFrom":makeQuery(id+"F3.opExtrude","CAP_EDGE",EDGE,{"disambiguationData":[OSD([sQuery(id+"F2.wireOp",EDGE,"E112.trimOffspring")])],"isStart":true})});
            var Q6;
            Q6=makeQuery(id+"F3.boolean.opBoolean","COPY",EDGE,{"derivedFrom":makeQuery(id+"F3.opExtrude","CAP_EDGE",EDGE,{"disambiguationData":[OSD([sQuery(id+"F2.wireOp",EDGE,"E113.trimOffspring")])],"isStart":true})});
            var Q7;
            Q7=makeQuery(id+"F3.boolean.opBoolean","COPY",EDGE,{"derivedFrom":makeQuery(id+"F3.opExtrude","CAP_EDGE",EDGE,{"disambiguationData":[OSD([sQuery(id+"F2.wireOp",EDGE,"E109.trimOffspring")])],"isStart":true})});
            var Q8;
            Q8=makeQuery(id+"F3.boolean.opBoolean","COPY",EDGE,{"derivedFrom":makeQuery(id+"F3.opExtrude","CAP_EDGE",EDGE,{"disambiguationData":[OSD([sQuery(id+"F2.wireOp",EDGE,"E108.trimOffspring")])],"isStart":true})});
            var Q9;
            {var subQ0=makeQuery(id+"F1.opExtrude","CAP_FACE",FACE,{"disambiguationData":[OSD([sQuery(id+"F0.wireOp",EDGE,"E0.bottom"),sQuery(id+"F0.wireOp",EDGE,"E0.top"),sQuery(id+"F0.wireOp",EDGE,"E0.left"),sQuery(id+"F0.wireOp",EDGE,"E0.right"),sQuery(id+"F0.wireOp",EDGE,"E1.filletArc"),sQuery(id+"F0.wireOp",EDGE,"E2.filletArc"),sQuery(id+"F0.wireOp",EDGE,"E3.filletArc"),sQuery(id+"F0.wireOp",EDGE,"E4.filletArc")])],"isStart":false});var subQ1=sQuery(id+"F2.wireOp",EDGE,"E108.trimOffspring");var subQ2=sQuery(id+"F2.wireOp",EDGE,"E107.trimOffspring");var subQ3=sQuery(id+"F4.wireOp",EDGE,"E114.top");var subQ4=sQuery(id+"F4.wireOp",EDGE,"E114.left");Q9=makeQuery(id+"F13.opFillet","BLEND_EDGE",EDGE,{"blendedFrom":[makeQuery(id+"F9.boolean.opBoolean","SPLIT",EDGE,{"disambiguationData":[TD([makeQuery(id+"F9.opExtrude","SWEPT_FACE",FACE,{"disambiguationData":[OSD([sQuery(id+"F6.wireOp",EDGE,"E130")])]})])],"derivedFrom":makeQuery(id+"F5.boolean.opBoolean","MERGE",EDGE,{"derivedFrom":[makeQuery(id+"F3.boolean.opBoolean","COPY",EDGE,{"derivedFrom":makeQuery(id+"F3.opExtrude","SWEPT_EDGE",EDGE,{"disambiguationData":[OSD([subQ2,subQ1])]})}),makeQuery(id+"F5.opExtrude","SWEPT_EDGE",EDGE,{"disambiguationData":[OSD([subQ3,subQ4])]})]})}),subQ0],"blendedInto":[subQ0]});}
            var Q10;
            Q10=makeQuery(id+"F3.boolean.opBoolean","COPY",EDGE,{"derivedFrom":makeQuery(id+"F3.opExtrude","CAP_EDGE",EDGE,{"disambiguationData":[OSD([sQuery(id+"F2.wireOp",EDGE,"E81.trimOffspring")])],"isStart":true})});
            var Q11;
            Q11=makeQuery(id+"F3.boolean.opBoolean","COPY",EDGE,{"derivedFrom":makeQuery(id+"F3.opExtrude","CAP_EDGE",EDGE,{"disambiguationData":[OSD([sQuery(id+"F2.wireOp",EDGE,"E54.trimOffspring")])],"isStart":true})});
            var Q12;
            Q12=makeQuery(id+"F3.boolean.opBoolean","COPY",EDGE,{"derivedFrom":makeQuery(id+"F3.opExtrude","CAP_EDGE",EDGE,{"disambiguationData":[OSD([sQuery(id+"F2.wireOp",EDGE,"E5.top")])],"isStart":true})});
            var Q13;
            Q13=makeQuery(id+"F3.boolean.opBoolean","COPY",EDGE,{"derivedFrom":makeQuery(id+"F3.opExtrude","CAP_EDGE",EDGE,{"disambiguationData":[OSD([sQuery(id+"F2.wireOp",EDGE,"E44.trimOffspring")])],"isStart":true})});
            var Q14;
            Q14=makeQuery(id+"F3.boolean.opBoolean","COPY",EDGE,{"derivedFrom":makeQuery(id+"F3.opExtrude","CAP_EDGE",EDGE,{"disambiguationData":[OSD([sQuery(id+"F2.wireOp",EDGE,"E39.trimOffspring")])],"isStart":true})});
            var Q15;
            Q15=makeQuery(id+"F3.boolean.opBoolean","COPY",EDGE,{"derivedFrom":makeQuery(id+"F3.opExtrude","CAP_EDGE",EDGE,{"disambiguationData":[OSD([sQuery(id+"F2.wireOp",EDGE,"E38.trimOffspring")])],"isStart":true})});
            var Q16;
            Q16=makeQuery(id+"F3.boolean.opBoolean","COPY",EDGE,{"derivedFrom":makeQuery(id+"F3.opExtrude","CAP_EDGE",EDGE,{"disambiguationData":[OSD([sQuery(id+"F2.wireOp",EDGE,"E31.trimOffspring")])],"isStart":true})});
            var Q17;
            Q17=makeQuery(id+"F3.boolean.opBoolean","COPY",EDGE,{"derivedFrom":makeQuery(id+"F3.opExtrude","CAP_EDGE",EDGE,{"disambiguationData":[OSD([sQuery(id+"F2.wireOp",EDGE,"E30.trimOffspring")])],"isStart":true})});
            var Q18;
            Q18=makeQuery(id+"F3.boolean.opBoolean","COPY",EDGE,{"derivedFrom":makeQuery(id+"F3.opExtrude","CAP_EDGE",EDGE,{"disambiguationData":[OSD([sQuery(id+"F2.wireOp",EDGE,"E5.left")])],"isStart":true})});
            fillet(context, id + "F14", {"entities" : qUnion([Q0, Q1, Q2, Q3, Q4, Q5, Q6, Q7, Q8, Q9, Q10, Q11, Q12, Q13, Q14, Q15, Q16, Q17, Q18]), "radius" : 2 * mm, "tangentPropagation" : true, "allowEdgeOverflow" : false});
        }
        {
            var Q0;
            Q0=makeQuery(id+"F1.opExtrude","CAP_FACE",FACE,{"disambiguationData":[OSD([sQuery(id+"F0.wireOp",EDGE,"E0.bottom"),sQuery(id+"F0.wireOp",EDGE,"E0.top"),sQuery(id+"F0.wireOp",EDGE,"E0.left"),sQuery(id+"F0.wireOp",EDGE,"E0.right"),sQuery(id+"F0.wireOp",EDGE,"E1.filletArc"),sQuery(id+"F0.wireOp",EDGE,"E2.filletArc"),sQuery(id+"F0.wireOp",EDGE,"E3.filletArc"),sQuery(id+"F0.wireOp",EDGE,"E4.filletArc")])],"isStart":false});
            var sketch = newSketch(context, id + "F15", { "sketchPlane" : qUnion([Q0])});
            skLineSegment(sketch, "E138.0", {"start": v(-180, 65) * mm, "end": v(180, 65) * mm});
            skLineSegment(sketch, "E139.0", {"start": v(-185, 60) * mm, "end": v(-185, -60) * mm});
            skArc(sketch, "E140.0", {"start": v(-180, 65) * mm, "mid": v(-183.54, 63.54) * mm, "end": v(-185, 60) * mm});
            skArc(sketch, "E141.0", {"start": v(-185, -60) * mm, "mid": v(-183.54, -63.54) * mm, "end": v(-180, -65) * mm});
            skLineSegment(sketch, "E142.0", {"start": v(-180, -65) * mm, "end": v(180, -65) * mm});
            skArc(sketch, "E143.0", {"start": v(180, -65) * mm, "mid": v(183.54, -63.54) * mm, "end": v(185, -60) * mm});
            skLineSegment(sketch, "E144.0", {"start": v(185, 60) * mm, "end": v(185, -60) * mm});
            skArc(sketch, "E145.0", {"start": v(-180, 67) * mm, "mid": v(-184.95, 64.95) * mm, "end": v(-187, 60) * mm});
            skLineSegment(sketch, "E145.1", {"start": v(-187, 60) * mm, "end": v(-187, -60) * mm});
            skLineSegment(sketch, "E145.2", {"start": v(-180, 67) * mm, "end": v(180, 67) * mm});
            skArc(sketch, "E145.3", {"start": v(-187, -60) * mm, "mid": v(-184.95, -64.95) * mm, "end": v(-180, -67) * mm});
            skArc(sketch, "E145.4", {"start": v(187, 60) * mm, "mid": v(184.95, 64.95) * mm, "end": v(180, 67) * mm});
            skLineSegment(sketch, "E145.5", {"start": v(187, 60) * mm, "end": v(187, -60) * mm});
            skArc(sketch, "E145.6", {"start": v(180, -67) * mm, "mid": v(184.95, -64.95) * mm, "end": v(187, -60) * mm});
            skLineSegment(sketch, "E145.7", {"start": v(-180, -67) * mm, "end": v(180, -67) * mm});
            skSolve(sketch);
        }
        {
            var Q0;
            Q0=makeQuery(id+"F15.imprint","IMPRINT",FACE,{"disambiguationData":[TD([[makeQuery(id+"F15.imprint","IMPRINT",EDGE,{"derivedFrom":sQuery(id+"F15.wireOp",EDGE,"E138.0")}),1.0]])]});
            extrude(context, id + "F16", {"entities" : qUnion([Q0]), "oppositeDirection" : true, "depth" : 1.5 * mm, "offsetDistance" : 25 * mm});
        }
        {
            var Q0;
            Q0=makeQuery(id+"F1.opExtrude","SWEPT_BODY",BODY,{"disambiguationData":[OSD([sQuery(id+"F0.wireOp",EDGE,"E0.bottom"),sQuery(id+"F0.wireOp",EDGE,"E0.top"),sQuery(id+"F0.wireOp",EDGE,"E0.left"),sQuery(id+"F0.wireOp",EDGE,"E0.right"),sQuery(id+"F0.wireOp",EDGE,"E1.filletArc"),sQuery(id+"F0.wireOp",EDGE,"E2.filletArc"),sQuery(id+"F0.wireOp",EDGE,"E3.filletArc"),sQuery(id+"F0.wireOp",EDGE,"E4.filletArc")])]});
            var Q1;
            Q1=makeQuery(id+"F16.opExtrude","SWEPT_BODY",BODY,{"disambiguationData":[OSD([sQuery(id+"F0.wireOp",EDGE,"E2.filletArc"),sQuery(id+"F15.wireOp",EDGE,"E138.0"),sQuery(id+"F15.wireOp",EDGE,"E139.0"),sQuery(id+"F15.wireOp",EDGE,"E140.0"),sQuery(id+"F15.wireOp",EDGE,"E141.0"),sQuery(id+"F15.wireOp",EDGE,"E142.0"),sQuery(id+"F15.wireOp",EDGE,"E143.0"),sQuery(id+"F15.wireOp",EDGE,"E144.0"),sQuery(id+"F15.wireOp",EDGE,"E145.0"),sQuery(id+"F15.wireOp",EDGE,"E145.1"),sQuery(id+"F15.wireOp",EDGE,"E145.2"),sQuery(id+"F15.wireOp",EDGE,"E145.3"),sQuery(id+"F15.wireOp",EDGE,"E145.4"),sQuery(id+"F15.wireOp",EDGE,"E145.5"),sQuery(id+"F15.wireOp",EDGE,"E145.6"),sQuery(id+"F15.wireOp",EDGE,"E145.7")])]});
            booleanBodies(context, id + "F17", {"operationType" : BooleanOperationType.UNION, "tools" : qUnion([Q0, Q1])});
        }
        {
            var Q0;
            Q0=makeQuery(id+"F9.boolean.opBoolean","MERGE",FACE,{"derivedFrom":[makeQuery(id+"F8.opExtrude","CAP_FACE",FACE,{"disambiguationData":[OSD([sQuery(id+"F7.wireOp",EDGE,"E135.bottom"),sQuery(id+"F7.wireOp",EDGE,"E135.top"),sQuery(id+"F7.wireOp",EDGE,"E135.left"),sQuery(id+"F7.wireOp",EDGE,"E135.right")])],"isStart":false}),makeQuery(id+"F8.opExtrude","CAP_FACE",FACE,{"disambiguationData":[OSD([sQuery(id+"F7.wireOp",EDGE,"E136.bottom"),sQuery(id+"F7.wireOp",EDGE,"E136.top"),sQuery(id+"F7.wireOp",EDGE,"E136.left"),sQuery(id+"F7.wireOp",EDGE,"E136.right")])],"isStart":false}),makeQuery(id+"F8.opExtrude","CAP_FACE",FACE,{"disambiguationData":[OSD([sQuery(id+"F7.wireOp",EDGE,"E137.bottom"),sQuery(id+"F7.wireOp",EDGE,"E137.top"),sQuery(id+"F7.wireOp",EDGE,"E137.left"),sQuery(id+"F7.wireOp",EDGE,"E137.right")])],"isStart":false}),makeQuery(id+"F9.opExtrude","SWEPT_FACE",FACE,{"disambiguationData":[OSD([sQuery(id+"F6.wireOp",EDGE,"E118")])]}),makeQuery(id+"F9.opExtrude","SWEPT_FACE",FACE,{"disambiguationData":[OSD([sQuery(id+"F6.wireOp",EDGE,"E122.0.1.2")])]}),makeQuery(id+"F9.opExtrude","SWEPT_FACE",FACE,{"disambiguationData":[OSD([sQuery(id+"F6.wireOp",EDGE,"E122.0.2.2")])]}),makeQuery(id+"F9.opExtrude","SWEPT_FACE",FACE,{"disambiguationData":[OSD([sQuery(id+"F6.wireOp",EDGE,"E122.0.3.2")])]}),makeQuery(id+"F9.opExtrude","SWEPT_FACE",FACE,{"disambiguationData":[OSD([sQuery(id+"F6.wireOp",EDGE,"E122.0.4.2")])]}),makeQuery(id+"F9.opExtrude","SWEPT_FACE",FACE,{"disambiguationData":[OSD([sQuery(id+"F6.wireOp",EDGE,"E126")])]}),makeQuery(id+"F9.opExtrude","SWEPT_FACE",FACE,{"disambiguationData":[OSD([sQuery(id+"F6.wireOp",EDGE,"E131")])]})]});
            var sketch = newSketch(context, id + "F18", { "sketchPlane" : qUnion([Q0])});
            skLineSegment(sketch, "E146", {"start": v(-1.5, 46.5) * mm, "end": v(-1.5, -46.5) * mm, "construction": true});
            skLineSegment(sketch, "E147.left", {"start": v(-1.5, -67) * mm, "end": v(-1.5, 67) * mm});
            skPoint(sketch, "E148.orphan", {"position": v(-180, 67) * mm});
            skPoint(sketch, "E149.orphan", {"position": v(-180, -67) * mm});
            skLineSegment(sketch, "E150.0", {"start": v(-1.5, -67) * mm, "end": v(-180, -67) * mm});
            skArc(sketch, "E151.0", {"start": v(-180, -67) * mm, "mid": v(-184.95, -64.95) * mm, "end": v(-187, -60) * mm});
            skLineSegment(sketch, "E152.0", {"start": v(-187, 60) * mm, "end": v(-187, -60) * mm});
            skArc(sketch, "E153.0", {"start": v(-187, 60) * mm, "mid": v(-184.95, 64.95) * mm, "end": v(-180, 67) * mm});
            skLineSegment(sketch, "E154.0", {"start": v(-1.5, 67) * mm, "end": v(-180, 67) * mm});
            skPoint(sketch, "E155.orphan", {"position": v(180, -67) * mm});
            skPoint(sketch, "E156.orphan", {"position": v(180, 67) * mm});
            skSolve(sketch);
        }
        {
            var Q0;
            Q0 = qSketchRegion(id + "F18", true);
            extrude(context, id + "F19", {"entities" : qUnion([Q0]), "operationType" : NewBodyOperationType.REMOVE, "endBound" : BoundingType.THROUGH_ALL, "oppositeDirection" : true, "depth" : 25 * mm, "offsetDistance" : 25 * mm});
        }
        {
            var Q0;
            Q0=makeQuery(id+"F19.boolean.opBoolean","COPY",FACE,{"derivedFrom":makeQuery(id+"F19.opExtrude","CAP_FACE",FACE,{"disambiguationData":[OSD([sQuery(id+"F18.wireOp",EDGE,"E147.left"),sQuery(id+"F18.wireOp",EDGE,"E150.0"),sQuery(id+"F18.wireOp",EDGE,"E151.0"),sQuery(id+"F18.wireOp",EDGE,"E152.0"),sQuery(id+"F18.wireOp",EDGE,"E153.0"),sQuery(id+"F18.wireOp",EDGE,"E154.0")])],"isStart":true})});
            var sketch = newSketch(context, id + "F20", { "sketchPlane" : qUnion([Q0])});
            skPoint(sketch, "E157.0", {"position": v(1.5, -47.25) * mm});
            skLineSegment(sketch, "E158.0", {"start": v(166, -48) * mm, "end": v(1.5, -48) * mm});
            skLineSegment(sketch, "E159.0", {"start": v(1.5, -46.5) * mm, "end": v(164.5, -46.5) * mm});
            skArc(sketch, "E160.0", {"start": v(166, -48) * mm, "mid": v(167.41, -47.41) * mm, "end": v(168, -46) * mm});
            skLineSegment(sketch, "E161.0", {"start": v(166.5, -44.5) * mm, "end": v(166.5, 44.5) * mm});
            skArc(sketch, "E162.0", {"start": v(164.5, -46.5) * mm, "mid": v(165.91, -45.91) * mm, "end": v(166.5, -44.5) * mm});
            skLineSegment(sketch, "E163.0", {"start": v(168, 46) * mm, "end": v(168, -46) * mm});
            skArc(sketch, "E164.0", {"start": v(166.5, 44.5) * mm, "mid": v(165.91, 45.91) * mm, "end": v(164.5, 46.5) * mm});
            skArc(sketch, "E165.0", {"start": v(168, 46) * mm, "mid": v(167.41, 47.41) * mm, "end": v(166, 48) * mm});
            skLineSegment(sketch, "E166.0", {"start": v(166, 48) * mm, "end": v(1.5, 48) * mm});
            skLineSegment(sketch, "E167.0", {"start": v(1.5, 46.5) * mm, "end": v(164.5, 46.5) * mm});
            skSolve(sketch);
        }
        {
            var Q0;
            Q0 = qSketchRegion(id + "F20", true);
            var Q1;
            Q1=makeQuery(id+"F20.imprint","IMPRINT",FACE,{"disambiguationData":[TD([[makeQuery(id+"F20.imprint","IMPRINT",EDGE,{"derivedFrom":sQuery(id+"F20.wireOp",EDGE,"E158.0")}),-1.0]])]});
            extrude(context, id + "F21", {"entities" : qUnion([Q0, Q1]), "operationType" : NewBodyOperationType.REMOVE, "endBound" : BoundingType.THROUGH_ALL, "oppositeDirection" : true, "depth" : 25 * mm, "offsetDistance" : 25 * mm});
        }
    });
